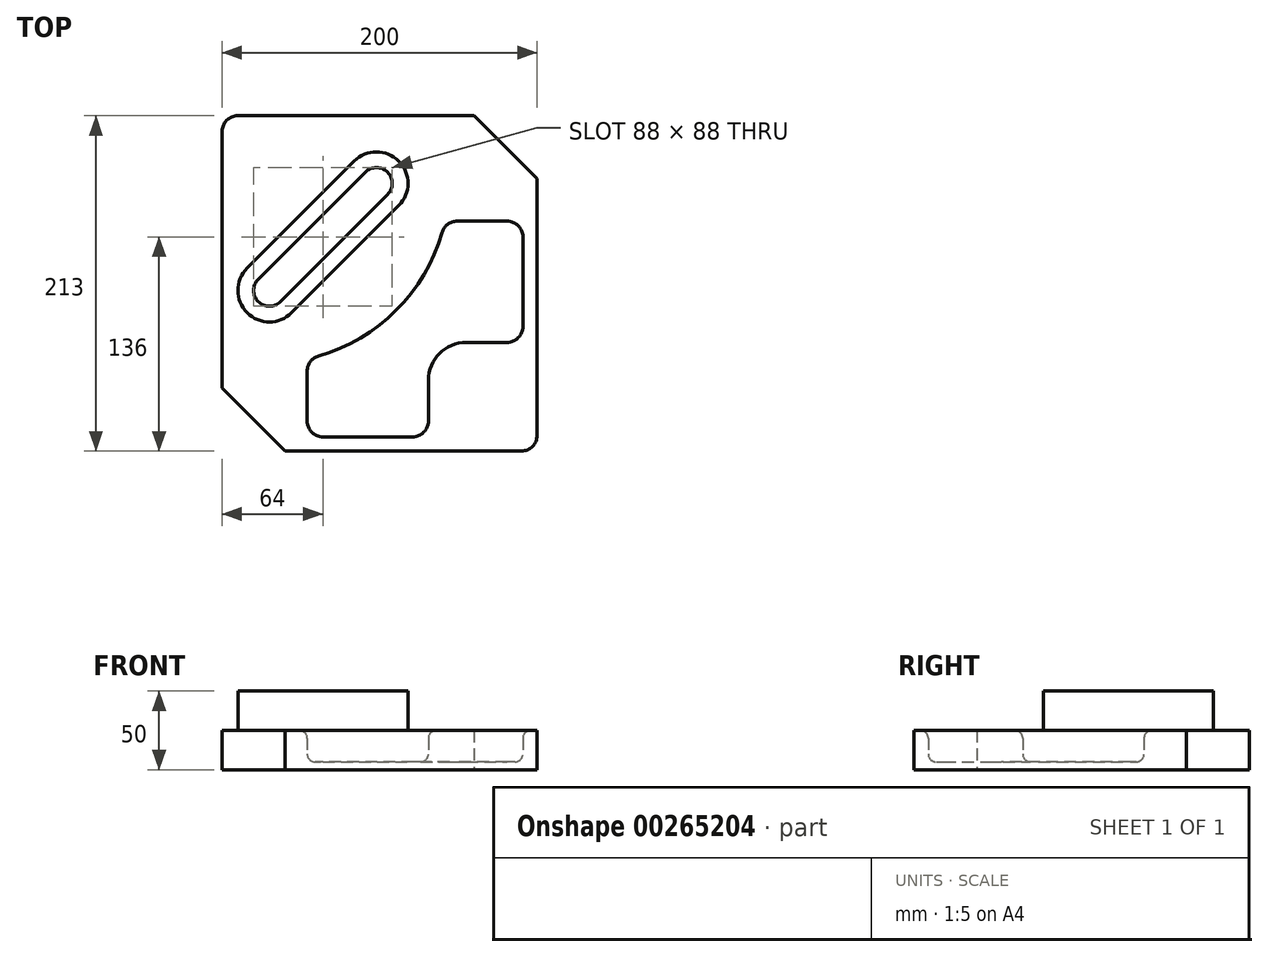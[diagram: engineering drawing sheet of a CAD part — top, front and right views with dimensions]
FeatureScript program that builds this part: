
annotation { "Feature Type Name" : "Feature", "Feature Type Description" : "" }
export const myFeature = defineFeature(function(context is Context, id is Id, definition is map)
    precondition{}
    {
        {
            var Q0;
            Q0=qCreatedBy(makeId("Top.planeOp"),FACE);
            var sketch = newSketch(context, id + "F0", { "sketchPlane" : qUnion([Q0])});
            skArc(sketch, "E0", {"start": v(31.26, -109.63) * mm, "mid": v(80.61, -80.61) * mm, "end": v(109.63, -31.26) * mm});
            skLineSegment(sketch, "E1", {"start": v(113.96, 3) * mm, "end": v(170, 3) * mm, "construction": true});
            skLineSegment(sketch, "E2", {"start": v(170, 3) * mm, "end": v(170, -160) * mm});
            skLineSegment(sketch, "E3", {"start": v(161, -170) * mm, "end": v(10, -170) * mm});
            skLineSegment(sketch, "E4", {"start": v(10, -170) * mm, "end": v(-30, -130) * mm});
            skLineSegment(sketch, "E5", {"start": v(170, 3) * mm, "end": v(130, 43) * mm});
            skLineSegment(sketch, "E6", {"start": v(-20, 43) * mm, "end": v(130, 43) * mm});
            skLineSegment(sketch, "E7", {"start": v(-30, 33) * mm, "end": v(-30, -130) * mm});
            skLineSegment(sketch, "E8", {"start": v(170, 3) * mm, "end": v(170, 43) * mm, "construction": true});
            skLineSegment(sketch, "E9", {"start": v(-30, -130) * mm, "end": v(-30, -170) * mm, "construction": true});
            skLineSegment(sketch, "E10", {"start": v(170, 0) * mm, "end": v(68, 0) * mm, "construction": true});
            skLineSegment(sketch, "E11", {"start": v(0, -170) * mm, "end": v(0, -68) * mm, "construction": true});
            skArc(sketch, "E12", {"start": v(82.14, -14.14) * mm, "mid": v(82.14, 14.14) * mm, "end": v(53.86, 14.14) * mm});
            skArc(sketch, "E13", {"start": v(75.07, -7.07) * mm, "mid": v(75.07, 7.07) * mm, "end": v(60.93, 7.07) * mm});
            skArc(sketch, "E14", {"start": v(-14.14, -53.86) * mm, "mid": v(-14.14, -82.14) * mm, "end": v(14.14, -82.14) * mm});
            skArc(sketch, "E15", {"start": v(-7.07, -60.93) * mm, "mid": v(-7.07, -75.07) * mm, "end": v(7.07, -75.07) * mm});
            skLineSegment(sketch, "E16", {"start": v(14.14, -82.14) * mm, "end": v(82.14, -14.14) * mm});
            skLineSegment(sketch, "E17", {"start": v(-14.14, -53.86) * mm, "end": v(53.86, 14.14) * mm});
            skLineSegment(sketch, "E18", {"start": v(7.07, -75.07) * mm, "end": v(75.07, -7.07) * mm});
            skLineSegment(sketch, "E19", {"start": v(-7.07, -60.93) * mm, "end": v(60.93, 7.07) * mm});
            skLineSegment(sketch, "E20", {"start": v(24, -151) * mm, "end": v(24, -119.25) * mm});
            skLineSegment(sketch, "E21", {"start": v(34, -161) * mm, "end": v(91, -161) * mm});
            skPoint(sketch, "E22.orphan", {"position": v(24, -170) * mm});
            skPoint(sketch, "E23.orphan", {"position": v(10, -161) * mm});
            skLineSegment(sketch, "E24", {"start": v(151, -24) * mm, "end": v(119.25, -24) * mm});
            skArc(sketch, "E25.trimOffspring", {"start": v(114, 0) * mm, "mid": v(114, 1.5) * mm, "end": v(113.96, 3) * mm});
            skLineSegment(sketch, "E26", {"start": v(161, -91) * mm, "end": v(161, -34) * mm});
            skPoint(sketch, "E27.orphan", {"position": v(161, -170) * mm});
            skPoint(sketch, "E28.orphan", {"position": v(170, -24) * mm});
            skLineSegment(sketch, "E29", {"start": v(101, -151) * mm, "end": v(101, -125) * mm});
            skLineSegment(sketch, "E30", {"start": v(125, -101) * mm, "end": v(151, -101) * mm});
            skPoint(sketch, "E31.orphan", {"position": v(170, -101) * mm});
            skPoint(sketch, "E32.orphan", {"position": v(101, -170) * mm});
            skArc(sketch, "E33", {"start": v(125, -101) * mm, "mid": v(108.03, -108.03) * mm, "end": v(101, -125) * mm});
            skArc(sketch, "E34", {"start": v(31.26, -109.63) * mm, "mid": v(26.02, -113.22) * mm, "end": v(24, -119.25) * mm});
            skArc(sketch, "E35", {"start": v(24, -151) * mm, "mid": v(26.93, -158.07) * mm, "end": v(34, -161) * mm});
            skArc(sketch, "E36", {"start": v(91, -161) * mm, "mid": v(98.07, -158.07) * mm, "end": v(101, -151) * mm});
            skArc(sketch, "E37", {"start": v(119.25, -24) * mm, "mid": v(113.22, -26.02) * mm, "end": v(109.63, -31.26) * mm});
            skArc(sketch, "E38", {"start": v(161, -34) * mm, "mid": v(158.07, -26.93) * mm, "end": v(151, -24) * mm});
            skArc(sketch, "E39", {"start": v(151, -101) * mm, "mid": v(158.07, -98.07) * mm, "end": v(161, -91) * mm});
            skArc(sketch, "E40", {"start": v(-20, 43) * mm, "mid": v(-27.07, 40.07) * mm, "end": v(-30, 33) * mm});
            skArc(sketch, "E41", {"start": v(160, -170) * mm, "mid": v(167.07, -167.07) * mm, "end": v(170, -160) * mm});
            skPoint(sketch, "E42.orphan", {"position": v(-30, 43) * mm});
            skPoint(sketch, "E43.orphan", {"position": v(170, -170) * mm});
            skSolve(sketch);
        }
        {
            var Q0;
            Q0=makeQuery(id+"F0.imprint","IMPRINT",FACE,{"disambiguationData":[TD([[makeQuery(id+"F0.imprint","IMPRINT",EDGE,{"derivedFrom":sQuery(id+"F0.wireOp",EDGE,"E0")}),1.0]])]});
            extrude(context, id + "F1", {"entities" : qUnion([Q0]), "depth" : 25 * mm});
        }
        {
            var Q0;
            Q0=makeQuery(id+"F1.opExtrude","CAP_FACE",FACE,{"disambiguationData":[OSD([sQuery(id+"F0.wireOp",EDGE,"E0"),sQuery(id+"F0.wireOp",EDGE,"E2"),sQuery(id+"F0.wireOp",EDGE,"E3"),sQuery(id+"F0.wireOp",EDGE,"E4"),sQuery(id+"F0.wireOp",EDGE,"E5"),sQuery(id+"F0.wireOp",EDGE,"E6"),sQuery(id+"F0.wireOp",EDGE,"E7"),sQuery(id+"F0.wireOp",EDGE,"E12"),sQuery(id+"F0.wireOp",EDGE,"E14"),sQuery(id+"F0.wireOp",EDGE,"E16"),sQuery(id+"F0.wireOp",EDGE,"E17"),sQuery(id+"F0.wireOp",EDGE,"E20"),sQuery(id+"F0.wireOp",EDGE,"E21"),sQuery(id+"F0.wireOp",EDGE,"E24"),sQuery(id+"F0.wireOp",EDGE,"E26"),sQuery(id+"F0.wireOp",EDGE,"E29"),sQuery(id+"F0.wireOp",EDGE,"E30"),sQuery(id+"F0.wireOp",EDGE,"E33"),sQuery(id+"F0.wireOp",EDGE,"E34"),sQuery(id+"F0.wireOp",EDGE,"E35"),sQuery(id+"F0.wireOp",EDGE,"E36"),sQuery(id+"F0.wireOp",EDGE,"E37"),sQuery(id+"F0.wireOp",EDGE,"E38"),sQuery(id+"F0.wireOp",EDGE,"E39"),sQuery(id+"F0.wireOp",EDGE,"E40"),sQuery(id+"F0.wireOp",EDGE,"E41")])],"isStart":true});
            var sketch = newSketch(context, id + "F2", { "sketchPlane" : qUnion([Q0])});
            skArc(sketch, "E44.0", {"start": v(24, 151) * mm, "mid": v(26.93, 158.07) * mm, "end": v(34, 161) * mm});
            skArc(sketch, "E44.1", {"start": v(31.26, 109.63) * mm, "mid": v(26.02, 113.22) * mm, "end": v(24, 119.25) * mm});
            skArc(sketch, "E44.2", {"start": v(160, 170) * mm, "mid": v(167.07, 167.07) * mm, "end": v(170, 160) * mm});
            skLineSegment(sketch, "E44.3", {"start": v(10, 170) * mm, "end": v(-30, 130) * mm});
            skLineSegment(sketch, "E44.4", {"start": v(-14.14, 53.86) * mm, "end": v(53.86, -14.14) * mm});
            skLineSegment(sketch, "E44.5", {"start": v(170, -3) * mm, "end": v(130, -43) * mm});
            skArc(sketch, "E44.6", {"start": v(91, 161) * mm, "mid": v(98.07, 158.07) * mm, "end": v(101, 151) * mm});
            skLineSegment(sketch, "E44.7", {"start": v(170, -3) * mm, "end": v(130, -43) * mm});
            skArc(sketch, "E44.8", {"start": v(82.14, 14.14) * mm, "mid": v(82.14, -14.14) * mm, "end": v(53.86, -14.14) * mm});
            skArc(sketch, "E44.9", {"start": v(151, 101) * mm, "mid": v(158.07, 98.07) * mm, "end": v(161, 91) * mm});
            skArc(sketch, "E44.10", {"start": v(160, 170) * mm, "mid": v(167.07, 167.07) * mm, "end": v(170, 160) * mm});
            skArc(sketch, "E44.11", {"start": v(125, 101) * mm, "mid": v(108.03, 108.03) * mm, "end": v(101, 125) * mm});
            skArc(sketch, "E44.12", {"start": v(-20, -43) * mm, "mid": v(-27.07, -40.07) * mm, "end": v(-30, -33) * mm});
            skArc(sketch, "E44.13", {"start": v(31.26, 109.63) * mm, "mid": v(80.61, 80.61) * mm, "end": v(109.63, 31.26) * mm});
            skArc(sketch, "E44.14", {"start": v(-14.14, 53.86) * mm, "mid": v(-14.14, 82.14) * mm, "end": v(14.14, 82.14) * mm});
            skLineSegment(sketch, "E44.15", {"start": v(14.14, 82.14) * mm, "end": v(82.14, 14.14) * mm});
            skLineSegment(sketch, "E45.0", {"start": v(-7.07, 60.93) * mm, "end": v(60.93, -7.07) * mm});
            skArc(sketch, "E46.0", {"start": v(-7.07, 60.93) * mm, "mid": v(-7.07, 75.07) * mm, "end": v(7.07, 75.07) * mm});
            skLineSegment(sketch, "E47.0", {"start": v(7.07, 75.07) * mm, "end": v(75.07, 7.07) * mm});
            skArc(sketch, "E48.0", {"start": v(75.07, 7.07) * mm, "mid": v(75.07, -7.07) * mm, "end": v(60.93, -7.07) * mm});
            skSolve(sketch);
        }
        {
            var Q0;
            Q0=makeQuery(id+"F2.imprint","IMPRINT",FACE,{"disambiguationData":[TD([[makeQuery(id+"F2.imprint","IMPRINT",EDGE,{"derivedFrom":sQuery(id+"F2.wireOp",EDGE,"E44.0")}),-1.0]])]});
            extrude(context, id + "F3", {"entities" : qUnion([Q0]), "operationType" : NewBodyOperationType.ADD, "oppositeDirection" : true, "depth" : 5 * mm});
        }
        {
            var Q0;
            Q0=makeQuery(id+"F2.imprint","IMPRINT",FACE,{"disambiguationData":[TD([[makeQuery(id+"F2.imprint","IMPRINT",EDGE,{"derivedFrom":sQuery(id+"F2.wireOp",EDGE,"E44.4")}),1.0]])]});
            extrude(context, id + "F4", {"entities" : qUnion([Q0]), "operationType" : NewBodyOperationType.ADD, "oppositeDirection" : true, "depth" : 50 * mm});
        }
        {
            var Q0;
            Q0=makeQuery(id+"F1.opExtrude","CAP_EDGE",EDGE,{"disambiguationData":[OSD([sQuery(id+"F0.wireOp",EDGE,"E17")])],"isStart":false});
            var Q1;
            Q1=makeQuery(id+"F3.opExtrude","CAP_FACE",FACE,{"disambiguationData":[OSD([sQuery(id+"F0.wireOp",EDGE,"E20"),sQuery(id+"F0.wireOp",EDGE,"E21"),sQuery(id+"F0.wireOp",EDGE,"E24"),sQuery(id+"F0.wireOp",EDGE,"E26"),sQuery(id+"F0.wireOp",EDGE,"E29"),sQuery(id+"F0.wireOp",EDGE,"E30"),sQuery(id+"F0.wireOp",EDGE,"E37"),sQuery(id+"F0.wireOp",EDGE,"E38"),sQuery(id+"F2.wireOp",EDGE,"E44.0"),sQuery(id+"F2.wireOp",EDGE,"E44.1"),sQuery(id+"F2.wireOp",EDGE,"E44.6"),sQuery(id+"F2.wireOp",EDGE,"E44.9"),sQuery(id+"F2.wireOp",EDGE,"E44.11"),sQuery(id+"F2.wireOp",EDGE,"E44.13")])],"isStart":false});
            var Q2;
            Q2=makeQuery(id+"F1.opExtrude","CAP_EDGE",EDGE,{"disambiguationData":[OSD([sQuery(id+"F0.wireOp",EDGE,"E33")])],"isStart":false});
            fillet(context, id + "F5", {"entities" : qUnion([Q0, Q1, Q2]), "radius" : 5 * mm, "tangentPropagation" : true, "allowEdgeOverflow" : false});
        }
    });
